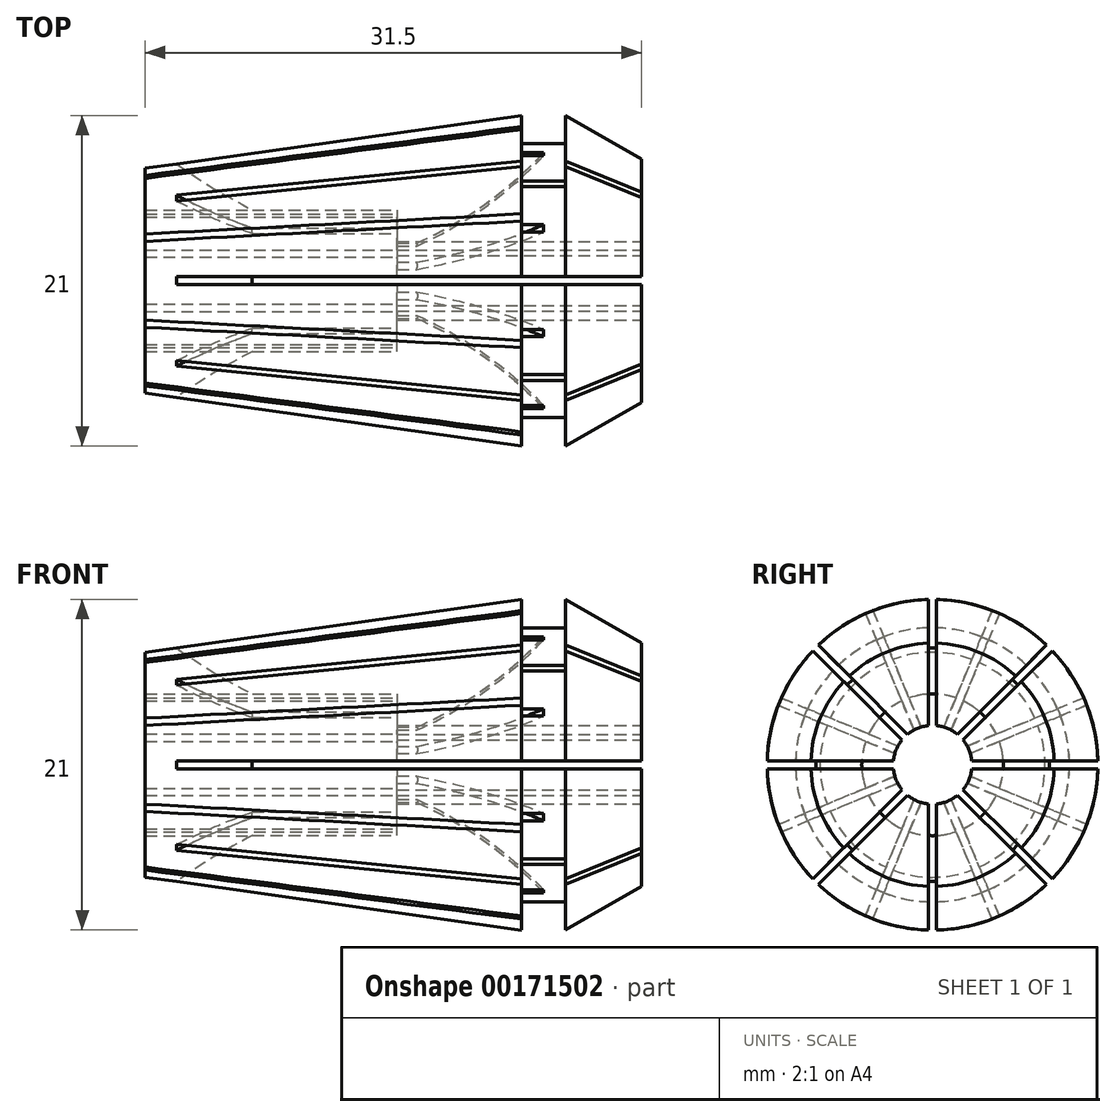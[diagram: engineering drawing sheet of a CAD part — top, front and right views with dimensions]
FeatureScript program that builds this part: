
annotation { "Feature Type Name" : "Feature", "Feature Type Description" : "" }
export const myFeature = defineFeature(function(context is Context, id is Id, definition is map)
    precondition{}
    {
        {
            assignVariable(context, id + "F0", {"name" : "s", "anyValue" : .5 * mm});
        }
        {
            var Q0;
            Q0=qCreatedBy(makeId("Front.planeOp"),FACE);
            var sketch = newSketch(context, id + "F1", { "sketchPlane" : qUnion([Q0])});
            skLineSegment(sketch, "E0", {"start": v(0, 0) * mm, "end": v(-18.8, 0) * mm, "construction": true});
            skLineSegment(sketch, "E1", {"start": v(0, 2.5) * mm, "end": v(-15.5, 2.5) * mm});
            skLineSegment(sketch, "E2", {"start": v(-15.5, 2.5) * mm, "end": v(-15.5, 4.5) * mm});
            skLineSegment(sketch, "E3", {"start": v(-15.5, 4.5) * mm, "end": v(-31.5, 4.5) * mm});
            skLineSegment(sketch, "E4", {"start": v(-31.5, 4.5) * mm, "end": v(-31.5, 7.14) * mm});
            skLineSegment(sketch, "E5", {"start": v(-31.5, 7.14) * mm, "end": v(-7.6, 10.5) * mm});
            skLineSegment(sketch, "E6", {"start": v(-7.6, 10.5) * mm, "end": v(-7.6, 8.7) * mm});
            skLineSegment(sketch, "E7", {"start": v(-7.6, 8.7) * mm, "end": v(-4.8, 8.7) * mm});
            skLineSegment(sketch, "E8", {"start": v(-4.8, 8.7) * mm, "end": v(-4.8, 10.5) * mm});
            skLineSegment(sketch, "E9", {"start": v(-4.8, 10.5) * mm, "end": v(0, 7.73) * mm});
            skLineSegment(sketch, "E10", {"start": v(0, 7.73) * mm, "end": v(0, 2.5) * mm});
            skPoint(sketch, "E11", {"position": v(-11.16, 10) * mm});
            skSolve(sketch);
        }
        {
            var Q0;
            Q0=makeQuery(id+"F1.imprint","IMPRINT",FACE,{"disambiguationData":[TD([[makeQuery(id+"F1.imprint","IMPRINT",EDGE,{"derivedFrom":sQuery(id+"F1.wireOp",EDGE,"E1")}),-1.0]])]});
            var Q1;
            Q1=sQuery(id+"F1.wireOp",EDGE,"E0");
            revolve(context, id + "F2", {"entities" : qUnion([Q0]), "axis" : qUnion([Q1]), "revolveType" : RevolveType.FULL});
        }
        {
            var Q0;
            Q0=qCreatedBy(makeId("Front.planeOp"),FACE);
            var sketch = newSketch(context, id + "F3", { "sketchPlane" : qUnion([Q0])});
            skArc(sketch, "E12", {"start": v(-29.52, 7.42) * mm, "mid": v(-22.83, 3.61) * mm, "end": v(-15.5, 1.25) * mm});
            skLineSegment(sketch, "E13", {"start": v(0, 0) * mm, "end": v(0, 1.25) * mm, "construction": true});
            skLineSegment(sketch, "E14", {"start": v(0, 1.25) * mm, "end": v(0, 2.5) * mm, "construction": true});
            skLineSegment(sketch, "E15", {"start": v(-15.5, 0) * mm, "end": v(-15.5, 1.25) * mm, "construction": true});
            skLineSegment(sketch, "E16", {"start": v(-15.5, 1.25) * mm, "end": v(-15.5, 2.5) * mm, "construction": true});
            skLineSegment(sketch, "E17", {"start": v(0, 1.25) * mm, "end": v(0, 7.73) * mm});
            skLineSegment(sketch, "E18", {"start": v(0, 7.73) * mm, "end": v(-4.8, 10.5) * mm});
            skLineSegment(sketch, "E19", {"start": v(-4.8, 10.5) * mm, "end": v(-7.6, 10.5) * mm});
            skLineSegment(sketch, "E20", {"start": v(-7.6, 10.5) * mm, "end": v(-29.52, 7.42) * mm});
            skLineSegment(sketch, "E21", {"start": v(-15.5, 1.25) * mm, "end": v(0, 1.25) * mm});
            skSolve(sketch);
        }
        {
            var Q0;
            Q0=makeQuery(id+"F3.imprint","IMPRINT",FACE,{"disambiguationData":[TD([[makeQuery(id+"F3.imprint","IMPRINT",EDGE,{"derivedFrom":sQuery(id+"F3.wireOp",EDGE,"E12")}),1.0]])]});
            extrude(context, id + "F4", {"entities" : qUnion([Q0]), "oppositeDirection" : true, "depth" : getVariable(context, 's') / 2, "hasSecondDirection" : true, "secondDirectionOppositeDirection" : false, "secondDirectionDepth" : getVariable(context, 's') / 2});
        }
        {
            var Q0;
            Q0=makeQuery(id+"F4.opExtrude","SWEPT_BODY",BODY,{"disambiguationData":[OSD([sQuery(id+"F3.wireOp",EDGE,"E12"),sQuery(id+"F3.wireOp",EDGE,"E17"),sQuery(id+"F3.wireOp",EDGE,"E18"),sQuery(id+"F3.wireOp",EDGE,"E19"),sQuery(id+"F3.wireOp",EDGE,"E20"),sQuery(id+"F3.wireOp",EDGE,"E21")])]});
            var Q1;
            Q1=sQuery(id+"F1.wireOp",EDGE,"E0");
            circularPattern(context, id + "F5", {"operationType" : NewBodyOperationType.REMOVE, "entities" : qUnion([Q0]), "axis" : qUnion([Q1]), "angle" : 360 * degree, "instanceCount" : 8, "equalSpace" : true, "computeTransformsWithoutBuiltin" : true});
        }
        {
            var Q0;
            Q0=qCreatedBy(makeId("Front.planeOp"),FACE);
            var sketch = newSketch(context, id + "F6", { "sketchPlane" : qUnion([Q0])});
            skArc(sketch, "E22", {"start": v(-15.5, 1.92) * mm, "mid": v(-10.45, 4.76) * mm, "end": v(-6.2, 8.7) * mm});
            skLineSegment(sketch, "E23", {"start": v(-7.6, 11.51) * mm, "end": v(-7.6, 8.7) * mm});
            skLineSegment(sketch, "E24", {"start": v(-7.6, 8.7) * mm, "end": v(-6.2, 8.7) * mm});
            skLineSegment(sketch, "E25", {"start": v(-31.5, 4) * mm, "end": v(-15.5, 4) * mm});
            skLineSegment(sketch, "E26", {"start": v(-15.5, 4) * mm, "end": v(-15.5, 1.92) * mm});
            skLineSegment(sketch, "E27", {"start": v(-31.5, 4) * mm, "end": v(-31.5, 8.15) * mm});
            skLineSegment(sketch, "E28", {"start": v(-31.5, 8.15) * mm, "end": v(-7.6, 11.51) * mm});
            skSolve(sketch);
        }
        {
            var Q0;
            Q0=qSketchRegion(id+"F6",true);
            extrude(context, id + "F7", {"entities" : qUnion([Q0]), "depth" : getVariable(context, 's') / 2, "hasSecondDirection" : true, "secondDirectionOppositeDirection" : true, "secondDirectionDepth" : getVariable(context, 's') / 2});
        }
        {
            var Q0;
            Q0=makeQuery(id+"F7.opExtrude","SWEPT_BODY",BODY,{"disambiguationData":[OSD([sQuery(id+"F6.wireOp",EDGE,"E22"),sQuery(id+"F6.wireOp",EDGE,"3NcqbOXm-ze6k-zp9A-J8Wp-eGL0M5BmVA6r"),sQuery(id+"F6.wireOp",EDGE,"E23"),sQuery(id+"F6.wireOp",EDGE,"E24"),sQuery(id+"F6.wireOp",EDGE,"CWTkhczA-MISY-V16c-OO6U-PYNv21l9aHGo"),sQuery(id+"F6.wireOp",EDGE,"E25"),sQuery(id+"F6.wireOp",EDGE,"E26")])]});
            var Q1;
            Q1=sQuery(id+"F1.wireOp",EDGE,"E0");
            transform(context, id + "F8", {"entities" : qUnion([Q0]), "transformType" : TransformType.ROTATION, "transformAxis" : qUnion([Q1]), "angle" : 22.5 * degree, "makeCopy" : false});
        }
        {
            var Q0;
            Q0=makeQuery(id+"F7.opExtrude","SWEPT_BODY",BODY,{"disambiguationData":[OSD([sQuery(id+"F6.wireOp",EDGE,"E22"),sQuery(id+"F6.wireOp",EDGE,"3NcqbOXm-ze6k-zp9A-J8Wp-eGL0M5BmVA6r"),sQuery(id+"F6.wireOp",EDGE,"E23"),sQuery(id+"F6.wireOp",EDGE,"E24"),sQuery(id+"F6.wireOp",EDGE,"CWTkhczA-MISY-V16c-OO6U-PYNv21l9aHGo"),sQuery(id+"F6.wireOp",EDGE,"E25"),sQuery(id+"F6.wireOp",EDGE,"E26")])]});
            var Q1;
            Q1=sQuery(id+"F1.wireOp",EDGE,"E0");
            circularPattern(context, id + "F9", {"operationType" : NewBodyOperationType.REMOVE, "entities" : qUnion([Q0]), "axis" : qUnion([Q1]), "angle" : 360 * degree, "instanceCount" : 8, "oppositeDirection" : true, "equalSpace" : true, "computeTransformsWithoutBuiltin" : true});
        }
    });
